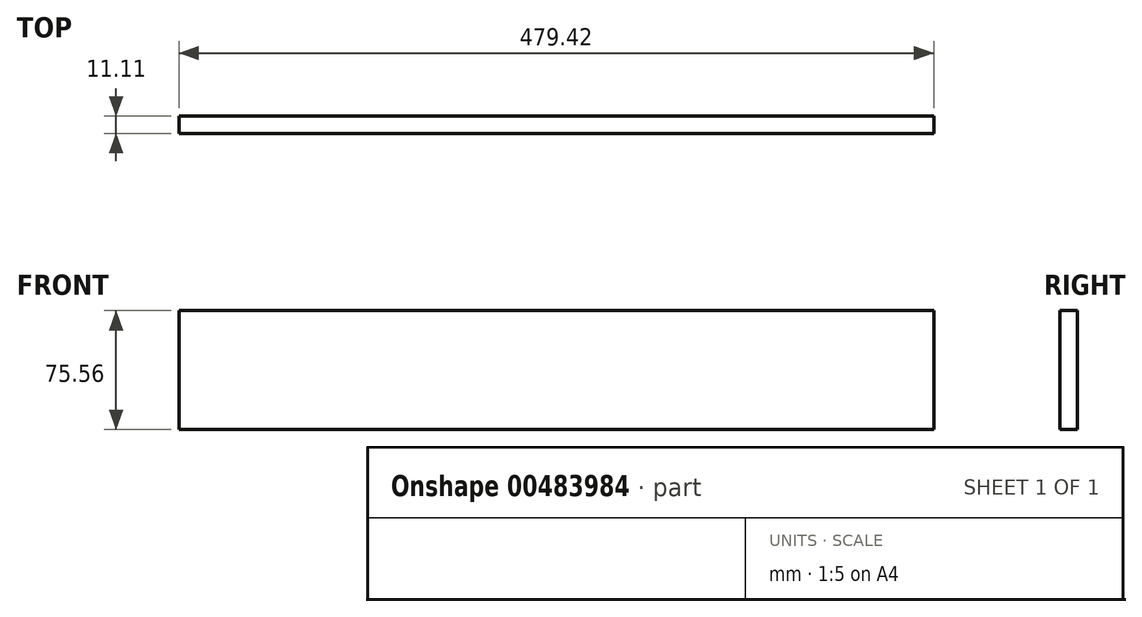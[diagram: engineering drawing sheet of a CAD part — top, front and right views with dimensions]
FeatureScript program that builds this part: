
annotation { "Feature Type Name" : "Feature", "Feature Type Description" : "" }
export const myFeature = defineFeature(function(context is Context, id is Id, definition is map)
    precondition{}
    {
        {
            var Q0;
            Q0=qCreatedBy(makeId("Front.planeOp"),FACE);
            var sketch = newSketch(context, id + "F0", { "sketchPlane" : qUnion([Q0])});
            skLineSegment(sketch, "E0.bottom", {"start": v(239.71, -37.78) * mm, "end": v(-239.71, -37.78) * mm});
            skLineSegment(sketch, "E0.top", {"start": v(239.71, 37.78) * mm, "end": v(-239.71, 37.78) * mm});
            skLineSegment(sketch, "E0.left", {"start": v(239.71, -37.78) * mm, "end": v(239.71, 37.78) * mm});
            skLineSegment(sketch, "E0.right", {"start": v(-239.71, -37.78) * mm, "end": v(-239.71, 37.78) * mm});
            skPoint(sketch, "E0.middle", {"position": v(0, 0) * mm});
            skSolve(sketch);
        }
        {
            var Q0;
            Q0 = qSketchRegion(id + "F0", true);
            extrude(context, id + "F1", {"entities" : qUnion([Q0]), "depth" : 11.1 * mm});
        }
    });
